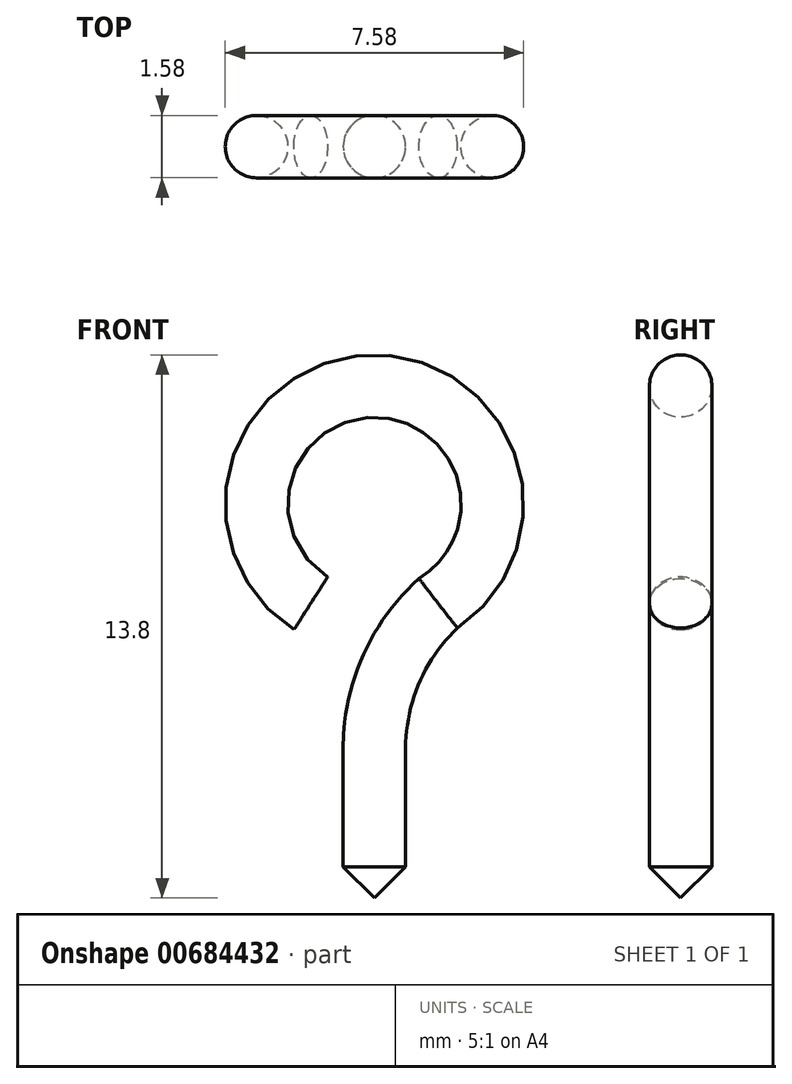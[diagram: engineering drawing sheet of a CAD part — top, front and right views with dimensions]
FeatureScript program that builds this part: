
annotation { "Feature Type Name" : "Feature", "Feature Type Description" : "" }
export const myFeature = defineFeature(function(context is Context, id is Id, definition is map)
    precondition{}
    {
        {
            var Q0;
            Q0=qCreatedBy(makeId("Top.planeOp"),FACE);
            var sketch = newSketch(context, id + "F0", { "sketchPlane" : qUnion([Q0])});
            skCircle(sketch, "E0", {"center": v(0, 0) * mm, "radius": 0.8 * mm});
            skSolve(sketch);
        }
        {
            var Q0;
            Q0=qCreatedBy(makeId("Front.planeOp"),FACE);
            var sketch = newSketch(context, id + "F1", { "sketchPlane" : qUnion([Q0])});
            skArc(sketch, "E1", {"start": v(1.62, 7.48) * mm, "mid": v(0, 13) * mm, "end": v(-1.62, 7.48) * mm});
            skLineSegment(sketch, "E2", {"start": v(0, 3.8) * mm, "end": v(0, 0) * mm});
            skPoint(sketch, "E3", {"position": v(0, 3.8) * mm});
            skArc(sketch, "E4", {"start": v(1.62, 7.48) * mm, "mid": v(0.42, 5.81) * mm, "end": v(0, 3.8) * mm});
            skSolve(sketch);
        }
        {
            var Q0;
            Q0=makeQuery(id+"F0.imprint","IMPRINT",FACE,{"disambiguationData":[TD([[makeQuery(id+"F0.imprint","IMPRINT",EDGE,{"derivedFrom":sQuery(id+"F0.wireOp",EDGE,"E0")}),1.0]])]});
            var Q1;
            Q1=sQuery(id+"F1.wireOp",EDGE,"E2");
            var Q2;
            Q2=sQuery(id+"F1.wireOp",EDGE,"E4");
            var Q3;
            Q3=sQuery(id+"F1.wireOp",EDGE,"E1");
            sweep(context, id + "F2", {"profiles" : qUnion([Q0]), "path" : qUnion([Q1, Q2, Q3])});
        }
        {
            var Q0;
            Q0=makeQuery(id+"F2.opSweep","CAP_EDGE",EDGE,{"disambiguationData":[OSD([sQuery(id+"F0.wireOp",EDGE,"E0"),sQuery(id+"F1.wireOp",VERTEX,"E2.end")])],"isStart":true});
            chamfer(context, id + "F3", {"entities" : qUnion([Q0]), "width" : 0.8 * mm, "tangentPropagation" : true});
        }
    });
